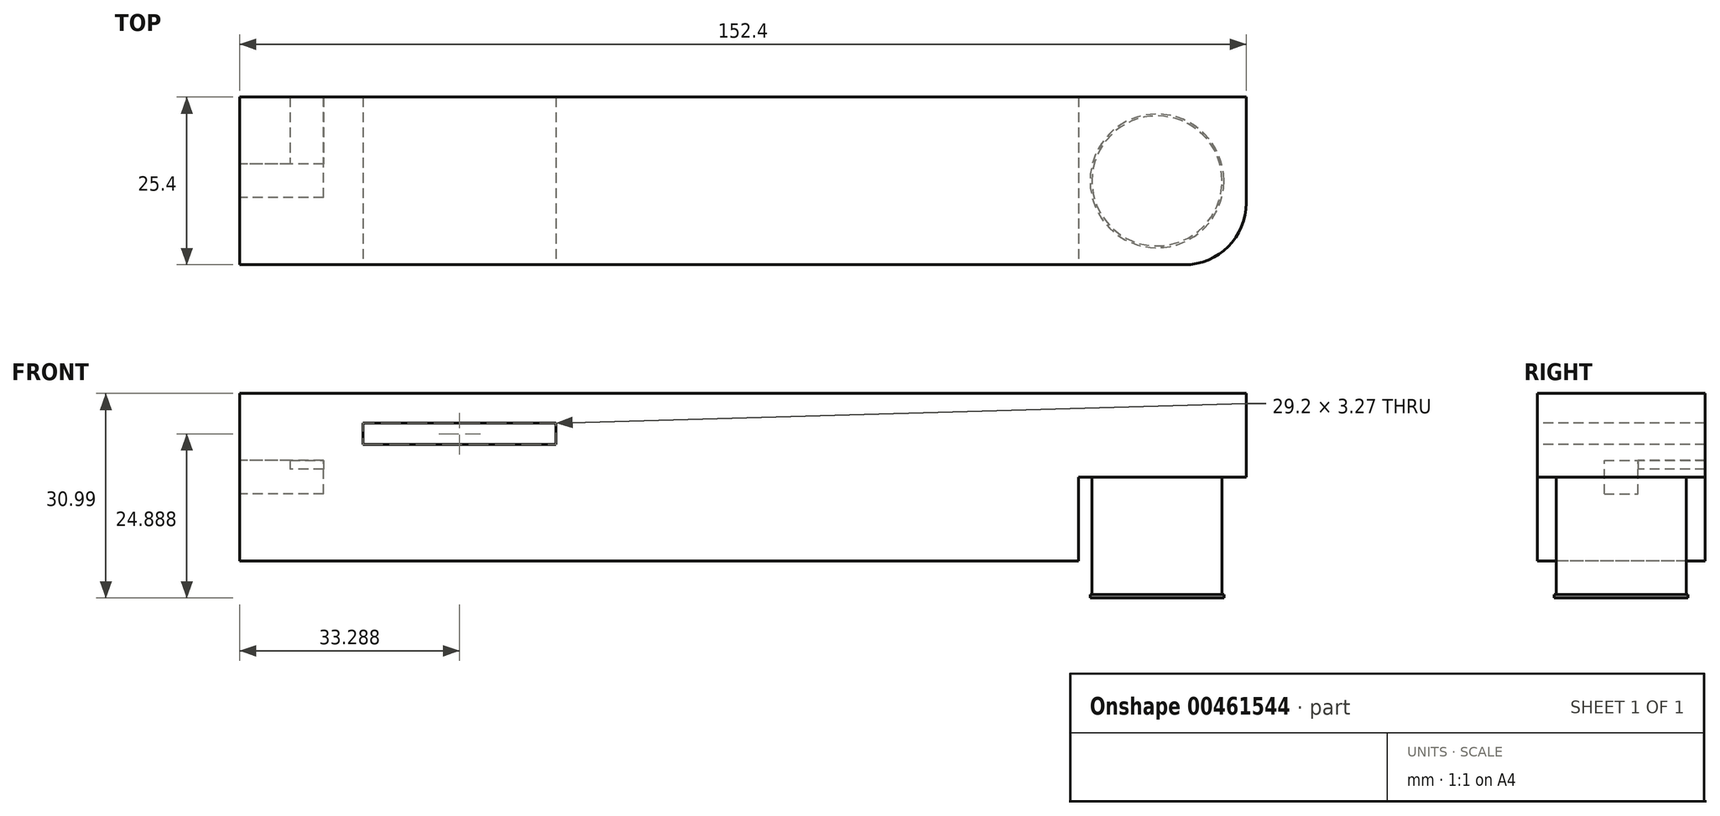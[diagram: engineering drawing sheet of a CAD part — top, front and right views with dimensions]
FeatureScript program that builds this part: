
annotation { "Feature Type Name" : "Feature", "Feature Type Description" : "" }
export const myFeature = defineFeature(function(context is Context, id is Id, definition is map)
    precondition{}
    {
        {
            var Q0;
            Q0=qCreatedBy(makeId("Top.planeOp"),FACE);
            var sketch = newSketch(context, id + "F0", { "sketchPlane" : qUnion([Q0])});
            skLineSegment(sketch, "E0.bottom", {"start": v(-76.2, 12.7) * mm, "end": v(76.2, 12.7) * mm});
            skLineSegment(sketch, "E0.top", {"start": v(-76.2, -12.7) * mm, "end": v(76.2, -12.7) * mm});
            skLineSegment(sketch, "E0.left", {"start": v(-76.2, 12.7) * mm, "end": v(-76.2, -12.7) * mm});
            skLineSegment(sketch, "E0.right", {"start": v(76.2, 12.7) * mm, "end": v(76.2, -12.7) * mm});
            skPoint(sketch, "E0.middle", {"position": v(0, 0) * mm});
            skSolve(sketch);
        }
        {
            var Q0;
            Q0=makeQuery(id+"F0.imprint","IMPRINT",FACE,{"disambiguationData":[TD([[makeQuery(id+"F0.imprint","IMPRINT",EDGE,{"derivedFrom":sQuery(id+"F0.wireOp",EDGE,"E0.bottom")}),-1.0]])]});
            extrude(context, id + "F1", {"entities" : qUnion([Q0]), "depth" : 25.4 * mm});
        }
        {
            var Q0;
            Q0=makeQuery(id+"F1.opExtrude","SWEPT_FACE",FACE,{"disambiguationData":[OSD([sQuery(id+"F0.wireOp",EDGE,"E0.right")])]});
            var sketch = newSketch(context, id + "F2", { "sketchPlane" : qUnion([Q0])});
            skLineSegment(sketch, "E1.bottom", {"start": v(-12.7, 0) * mm, "end": v(12.7, 0) * mm});
            skLineSegment(sketch, "E1.top", {"start": v(-12.7, 16.8) * mm, "end": v(12.7, 16.8) * mm});
            skLineSegment(sketch, "E1.left", {"start": v(-12.7, 0) * mm, "end": v(-12.7, 16.8) * mm});
            skLineSegment(sketch, "E1.right", {"start": v(12.7, 0) * mm, "end": v(12.7, 16.8) * mm});
            skSolve(sketch);
        }
        {
            var Q0;
            Q0=qCreatedBy(makeId("Right.planeOp"),FACE);
            var sketch = newSketch(context, id + "F3", { "sketchPlane" : qUnion([Q0])});
            skSolve(sketch);
        }
        {
            var Q0;
            Q0 = qSketchRegion(id + "F3", true);
            var Q1;
            Q1=makeQuery(id+"F2.imprint","IMPRINT",FACE,{"disambiguationData":[TD([[makeQuery(id+"F2.imprint","IMPRINT",EDGE,{"derivedFrom":sQuery(id+"F2.wireOp",EDGE,"E1.bottom")}),-1.0]])]});
            extrude(context, id + "F4", {"entities" : qUnion([Q0, Q1]), "operationType" : NewBodyOperationType.ADD, "oppositeDirection" : true, "depth" : 3.45 * mm});
        }
        {
            var Q0;
            Q0=makeQuery(id+"F1.opExtrude","SWEPT_FACE",FACE,{"disambiguationData":[OSD([sQuery(id+"F0.wireOp",EDGE,"E0.right")])]});
            var sketch = newSketch(context, id + "F5", { "sketchPlane" : qUnion([Q0])});
            skLineSegment(sketch, "E2.bottom", {"start": v(-12.7, 25.4) * mm, "end": v(12.7, 25.4) * mm});
            skLineSegment(sketch, "E2.top", {"start": v(-12.7, 12.7) * mm, "end": v(12.7, 12.7) * mm});
            skLineSegment(sketch, "E2.left", {"start": v(-12.7, 25.4) * mm, "end": v(-12.7, 12.7) * mm});
            skLineSegment(sketch, "E2.right", {"start": v(12.7, 25.4) * mm, "end": v(12.7, 12.7) * mm});
            skSolve(sketch);
        }
        {
            var Q0;
            {var subQ0=sQuery(id+"F5.wireOp",EDGE,"E2.top");Q0=makeQuery(id+"F5.imprint","IMPRINT",FACE,{"disambiguationData":[TD([[makeQuery(id+"F5.imprint","IMPRINT",EDGE,{"derivedFrom":subQ0}),-1.0]])]});}
            extrude(context, id + "F6", {"entities" : qUnion([Q0]), "operationType" : NewBodyOperationType.REMOVE, "oppositeDirection" : true, "depth" : 25.4 * mm});
        }
        {
            var Q0;
            Q0=makeQuery(id+"F6.boolean.opBoolean","COPY",FACE,{"derivedFrom":makeQuery(id+"F6.opExtrude","SWEPT_FACE",FACE,{"disambiguationData":[OSD([sQuery(id+"F5.wireOp",EDGE,"E2.top")])]})});
            var sketch = newSketch(context, id + "F7", { "sketchPlane" : qUnion([Q0])});
            skCircle(sketch, "E3", {"center": v(62.7, 0) * mm, "radius": 9.85 * mm});
            skSolve(sketch);
        }
        {
            var Q0;
            Q0=makeQuery(id+"F1.opExtrude","SWEPT_FACE",FACE,{"disambiguationData":[OSD([sQuery(id+"F0.wireOp",EDGE,"E0.top")])]});
            var sketch = newSketch(context, id + "F8", { "sketchPlane" : qUnion([Q0])});
            skLineSegment(sketch, "E4.bottom", {"start": v(-57.51, 20.94) * mm, "end": v(-28.31, 20.94) * mm});
            skLineSegment(sketch, "E4.top", {"start": v(-57.51, 17.66) * mm, "end": v(-28.31, 17.66) * mm});
            skLineSegment(sketch, "E4.left", {"start": v(-57.51, 20.94) * mm, "end": v(-57.51, 17.66) * mm});
            skLineSegment(sketch, "E4.right", {"start": v(-28.31, 20.94) * mm, "end": v(-28.31, 17.66) * mm});
            skSolve(sketch);
        }
        {
            var Q0;
            Q0=makeQuery(id+"F8.imprint","IMPRINT",FACE,{"disambiguationData":[TD([[makeQuery(id+"F8.imprint","IMPRINT",EDGE,{"derivedFrom":sQuery(id+"F8.wireOp",EDGE,"E4.bottom")}),-1.0]])]});
            extrude(context, id + "F9", {"entities" : qUnion([Q0]), "operationType" : NewBodyOperationType.REMOVE, "oppositeDirection" : true, "depth" : 25.4 * mm});
        }
        {
            var Q0;
            Q0=makeQuery(id+"F1.opExtrude","SWEPT_EDGE",EDGE,{"disambiguationData":[OSD([sQuery(id+"F0.wireOp",EDGE,"E0.top"),sQuery(id+"F0.wireOp",EDGE,"E0.right")])]});
            fillet(context, id + "F10", {"entities" : qUnion([Q0]), "radius" : 9.38 * mm, "tangentPropagation" : true, "allowEdgeOverflow" : false});
        }
        {
            var Q0;
            Q0=makeQuery(id+"F7.imprint","IMPRINT",FACE,{"disambiguationData":[TD([[makeQuery(id+"F7.imprint","IMPRINT",EDGE,{"derivedFrom":sQuery(id+"F7.wireOp",EDGE,"E3")}),1.0]])]});
            extrude(context, id + "F11", {"entities" : qUnion([Q0]), "operationType" : NewBodyOperationType.ADD, "depth" : 17.78 * mm});
        }
        {
            var Q0;
            Q0=makeQuery(id+"F11.opExtrude","CAP_FACE",FACE,{"disambiguationData":[OSD([sQuery(id+"F7.wireOp",EDGE,"E3")])],"isStart":false});
            var sketch = newSketch(context, id + "F12", { "sketchPlane" : qUnion([Q0])});
            skCircle(sketch, "E5", {"center": v(62.7, 0) * mm, "radius": 10.13 * mm});
            skSolve(sketch);
        }
        {
            var Q0;
            Q0=makeQuery(id+"F12.imprint","IMPRINT",FACE,{"disambiguationData":[TD([[makeQuery(id+"F12.imprint","IMPRINT",EDGE,{"derivedFrom":sQuery(id+"F12.wireOp",EDGE,"E5")}),1.0]])]});
            var Q1;
            Q1=makeQuery(id+"F12.imprint","IMPRINT",FACE,{"disambiguationData":[TD([[makeQuery(id+"F12.imprint","IMPRINT",EDGE,{"derivedFrom":makeQuery(id+"F11.opExtrude","CAP_EDGE",EDGE,{"disambiguationData":[OSD([sQuery(id+"F7.wireOp",EDGE,"E3")])],"isStart":false})}),1.0]])]});
            var Q2;
            Q2=makeQuery(id+"F11.opExtrude","CAP_FACE",FACE,{"disambiguationData":[OSD([sQuery(id+"F7.wireOp",EDGE,"E3")])],"isStart":false});
            extrude(context, id + "F13", {"entities" : qUnion([Q0, Q1, Q2]), "operationType" : NewBodyOperationType.ADD, "depth" : 0.5 * mm});
        }
        {
            var Q0;
            Q0=makeQuery(id+"F1.opExtrude","SWEPT_FACE",FACE,{"disambiguationData":[OSD([sQuery(id+"F0.wireOp",EDGE,"E0.left")])]});
            var sketch = newSketch(context, id + "F14", { "sketchPlane" : qUnion([Q0])});
            skLineSegment(sketch, "E6.bottom", {"start": v(2.54, 10.16) * mm, "end": v(-2.54, 10.16) * mm});
            skLineSegment(sketch, "E6.top", {"start": v(2.54, 15.24) * mm, "end": v(-2.54, 15.24) * mm});
            skLineSegment(sketch, "E6.left", {"start": v(2.54, 10.16) * mm, "end": v(2.54, 15.24) * mm});
            skLineSegment(sketch, "E6.right", {"start": v(-2.54, 10.16) * mm, "end": v(-2.54, 15.24) * mm});
            skPoint(sketch, "E6.middle", {"position": v(0, 12.7) * mm});
            skPoint(sketch, "E6.middle.positionSnap0", {"position": v(12.7, 12.7) * mm});
            skPoint(sketch, "E6.centerSnap0", {"position": v(12.7, 12.7) * mm});
            skSolve(sketch);
        }
        {
            var Q0;
            Q0=makeQuery(id+"F14.imprint","IMPRINT",FACE,{"disambiguationData":[TD([[makeQuery(id+"F14.imprint","IMPRINT",EDGE,{"derivedFrom":sQuery(id+"F14.wireOp",EDGE,"E6.bottom")}),-1.0]])]});
            extrude(context, id + "F15", {"entities" : qUnion([Q0]), "operationType" : NewBodyOperationType.REMOVE, "oppositeDirection" : true, "depth" : 12.7 * mm});
        }
        {
            var Q0;
            Q0=makeQuery(id+"F15.boolean.opBoolean","COPY",FACE,{"derivedFrom":makeQuery(id+"F15.opExtrude","SWEPT_FACE",FACE,{"disambiguationData":[OSD([sQuery(id+"F14.wireOp",EDGE,"E6.right")])]})});
            var sketch = newSketch(context, id + "F16", { "sketchPlane" : qUnion([Q0])});
            skLineSegment(sketch, "E7.bottom", {"start": v(-63.5, 15.24) * mm, "end": v(-68.57, 15.24) * mm});
            skLineSegment(sketch, "E7.top", {"start": v(-63.5, 13.97) * mm, "end": v(-68.57, 13.97) * mm});
            skLineSegment(sketch, "E7.left", {"start": v(-63.5, 15.24) * mm, "end": v(-63.5, 13.97) * mm});
            skLineSegment(sketch, "E7.right", {"start": v(-68.57, 15.24) * mm, "end": v(-68.57, 13.97) * mm});
            skSolve(sketch);
        }
        {
            var Q0;
            Q0=makeQuery(id+"F16.imprint","IMPRINT",FACE,{"disambiguationData":[TD([[makeQuery(id+"F16.imprint","IMPRINT",EDGE,{"derivedFrom":sQuery(id+"F16.wireOp",EDGE,"E7.bottom")}),1.0]])]});
            extrude(context, id + "F17", {"entities" : qUnion([Q0]), "operationType" : NewBodyOperationType.REMOVE, "oppositeDirection" : true, "depth" : 12.7 * mm});
        }
    });
